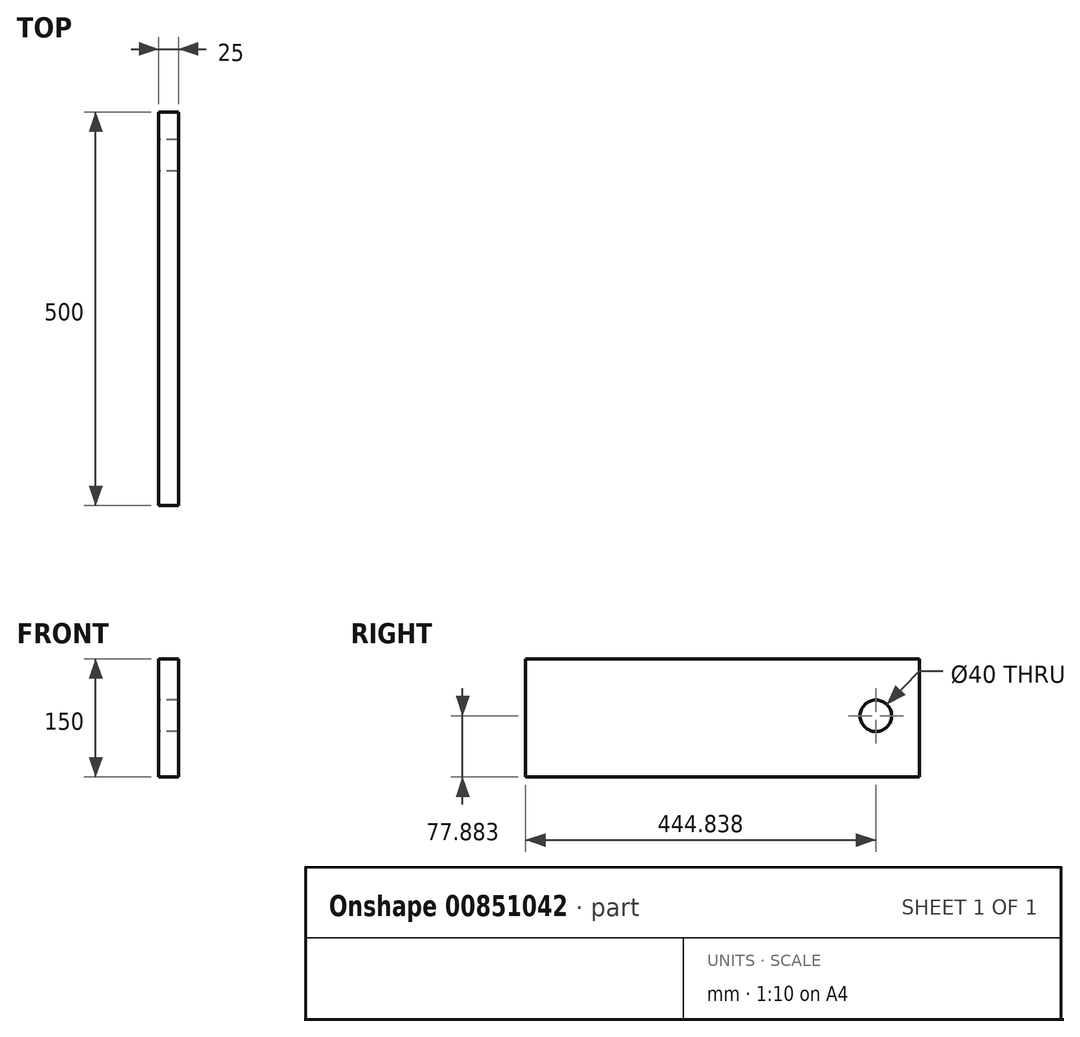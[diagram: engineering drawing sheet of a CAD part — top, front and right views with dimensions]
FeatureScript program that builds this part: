
annotation { "Feature Type Name" : "Feature", "Feature Type Description" : "" }
export const myFeature = defineFeature(function(context is Context, id is Id, definition is map)
    precondition{}
    {
        {
            var Q0;
            Q0=qCreatedBy(makeId("Right.planeOp"),FACE);
            var sketch = newSketch(context, id + "F0", { "sketchPlane" : qUnion([Q0])});
            skLineSegment(sketch, "E0.bottom", {"start": v(-57.17, 94.56) * mm, "end": v(442.83, 94.56) * mm});
            skLineSegment(sketch, "E0.top", {"start": v(-57.17, -55.44) * mm, "end": v(442.83, -55.44) * mm});
            skLineSegment(sketch, "E0.left", {"start": v(-57.17, 94.56) * mm, "end": v(-57.17, -55.44) * mm});
            skLineSegment(sketch, "E0.right", {"start": v(442.83, 94.56) * mm, "end": v(442.83, -55.44) * mm});
            skCircle(sketch, "E1", {"center": v(387.67, 22.44) * mm, "radius": 20 * mm});
            skSolve(sketch);
        }
        {
            var Q0;
            Q0=makeQuery(id+"F0.imprint","IMPRINT",FACE,{"disambiguationData":[TD([[makeQuery(id+"F0.imprint","IMPRINT",EDGE,{"derivedFrom":sQuery(id+"F0.wireOp",EDGE,"E0.bottom")}),-1.0]])]});
            extrude(context, id + "F1", {"entities" : qUnion([Q0]), "depth" : 25 * mm, "offsetDistance" : 25 * mm});
        }
    });
